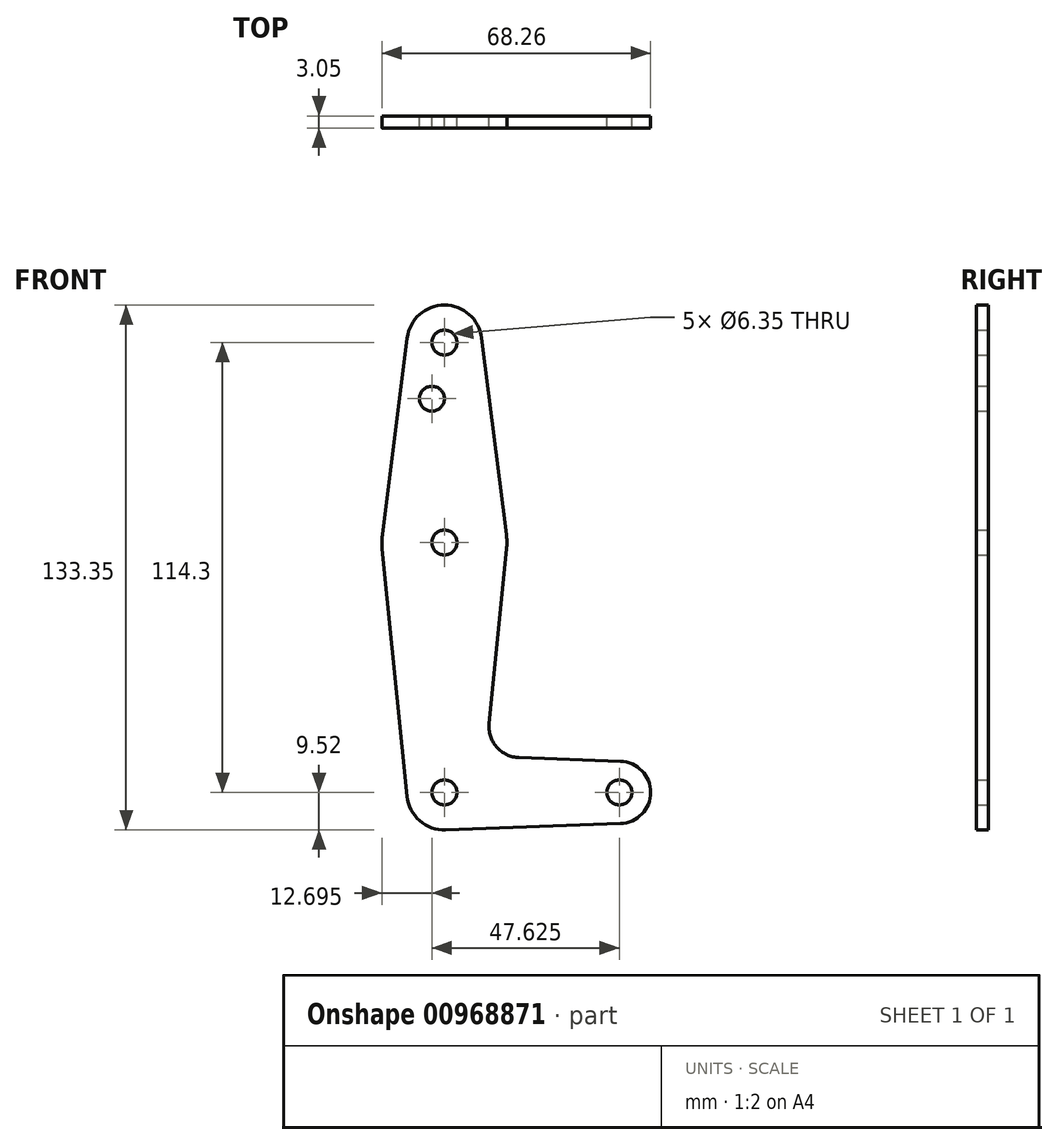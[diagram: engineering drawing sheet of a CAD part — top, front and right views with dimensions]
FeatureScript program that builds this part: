
annotation { "Feature Type Name" : "Feature", "Feature Type Description" : "" }
export const myFeature = defineFeature(function(context is Context, id is Id, definition is map)
    precondition{}
    {
        {
            var Q0;
            Q0=qCreatedBy(makeId("Front.planeOp"),FACE);
            var sketch = newSketch(context, id + "F0", { "sketchPlane" : qUnion([Q0])});
            skCircle(sketch, "E0", {"center": v(0, 0) * mm, "radius": 9.53 * mm});
            skLineSegment(sketch, "E1", {"start": v(0, 0) * mm, "end": v(0, 114.3) * mm, "construction": true});
            skCircle(sketch, "E2", {"center": v(0, 114.3) * mm, "radius": 9.53 * mm});
            skCircle(sketch, "E3", {"center": v(0, 63.5) * mm, "radius": 15.88 * mm});
            skLineSegment(sketch, "E4", {"start": v(0, 0) * mm, "end": v(44.45, 0) * mm, "construction": true});
            skCircle(sketch, "E5", {"center": v(44.45, 0) * mm, "radius": 7.94 * mm});
            skLineSegment(sketch, "E6", {"start": v(-9.45, 115.5) * mm, "end": v(-15.75, 65.48) * mm});
            skLineSegment(sketch, "E7", {"start": v(9.45, 115.5) * mm, "end": v(15.75, 65.48) * mm});
            skLineSegment(sketch, "E8", {"start": v(15.8, 61.91) * mm, "end": v(11.34, 17.59) * mm});
            skLineSegment(sketch, "E9", {"start": v(44.73, -7.93) * mm, "end": v(0, -9.53) * mm});
            skLineSegment(sketch, "E10", {"start": v(18.97, 8.85) * mm, "end": v(44.73, 7.93) * mm});
            skCircle(sketch, "E11", {"center": v(0, 114.3) * mm, "radius": 3.18 * mm});
            skCircle(sketch, "E12", {"center": v(-3.17, 100.03) * mm, "radius": 3.18 * mm});
            skCircle(sketch, "E13", {"center": v(0, 63.5) * mm, "radius": 3.18 * mm});
            skCircle(sketch, "E14", {"center": v(0, 0) * mm, "radius": 3.18 * mm});
            skCircle(sketch, "E15", {"center": v(44.45, 0) * mm, "radius": 3.18 * mm});
            skArc(sketch, "E16.filletArc", {"start": v(11.34, 17.59) * mm, "mid": v(13.26, 11.57) * mm, "end": v(18.97, 8.85) * mm});
            skPoint(sketch, "E17.end.orphan", {"position": v(-9.53, 0) * mm});
            skLineSegment(sketch, "E18", {"start": v(-9.48, -0.95) * mm, "end": v(-15.8, 61.91) * mm});
            skSolve(sketch);
        }
        {
            var Q0;
            Q0 = qSketchRegion(id + "F0", true);
            extrude(context, id + "F1", {"entities" : qUnion([Q0]), "depth" : 3.05 * mm, "offsetDistance" : 25.4 * mm});
        }
    });
